# Revit family: Doors_Garage_Asta-America_300-Series
name_source: partatom
category: Doors
units: mm (PartAtom-declared; Revit-internal decimal feet)

## family parameters
Always vertical = Yes
Classification Number = 23.30.10.17.27.11
Cut with Voids When Loaded = No
Host = Wall
Room Calculation Point = No
Shared = No

## types (4) — shared parameters
Analytic Construction = <None>
Assembly Code = B2030400
Bottom Bar = Asta America - Steel
Curtain Slats = Asta America - Steel - Powder Coat - Grey Topcoat
Description = ASTA AMERICA 300 Series Commercial Slat Doors
Edition number = 1
Flat Slat = Yes
Function = Exterior
Guides = Asta America - Steel
Height = 10' - 0"
Keynote = 08110
Manufacturer = Asta America
Model = 300 Series Commercial Slat Doors
Opening Height = 10' - 0"
Opening Width = 8' - 0"
Product Guid = 993f9d3d-4a5d-4874-89c9-48cf8775287c
Product data url = https://www.bimobject.com
Rough Height = 10' - 0"
Rough Width = 8' - 0"
URL = www.astaamerica.com
Wall Closure = By host
Width = 8' - 0"
Windload = Door construction designed to satisfy windload of +74.4/-69.8psf for sizes up to 12’0” wide by 14’0” high. Consult factory for available
sizes or higher windload.
v = 1' - 11"
x = 1' - 11"
z_Bottom Profile = 7' - 11 1/2"
z_Curved Array Height = 12' - 4"
z_Curved Slat = No
z_Height Control = 10' - 0"
z_Motor Width = 8' - 4 1/2"
z_Offset = 0' - 1"
z_Part Slat Number = 27
z_Slat Height = 0' - 2 1/2"
z_Slat Number = 51
z_Slat Offset = 4' - 2 1/2"
z_Structural Steel Guide = 10' - 8 1/2"
z_Third Array Height = 5' - 2"
z_Width Control = 8' - 0"

## per-type parameters (varying)
| type | z_A1 | z_A2 | z_Chain | z_Commercial Operator | z_Slat Door2 | z_Structural Steel Guide Visibility |
| Slat Door & Operator | 0' - 11" | 6' - 0" | No | Yes | Yes | No |
| Slat Door Chain Hoist | 0' - 10" | 6' - 0" | Yes | No | Yes | No |
| Structural Steel Guides and Chain Hoist | 0' - 10" | 0' - 6" | Yes | No | No | Yes |
| Structural Steel Guides & Operator | 0' - 11 1/2" | 6' - 0" | No | Yes | No | Yes |

## geometry (parser evidence)
native form markers: Sweep x31
no freeform markers — native parametric forms only
